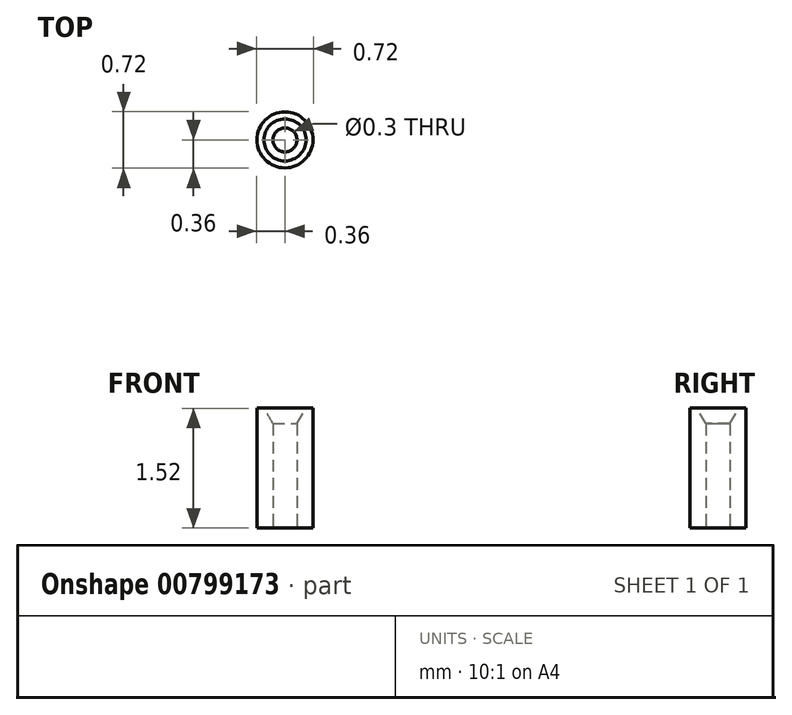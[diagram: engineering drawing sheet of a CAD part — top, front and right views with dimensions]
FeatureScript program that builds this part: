
annotation { "Feature Type Name" : "Feature", "Feature Type Description" : "" }
export const myFeature = defineFeature(function(context is Context, id is Id, definition is map)
    precondition{}
    {
        {
            var Q0;
            Q0=qCreatedBy(makeId("Front.planeOp"),FACE);
            var sketch = newSketch(context, id + "F0", { "sketchPlane" : qUnion([Q0])});
            skLineSegment(sketch, "E0", {"start": v(0.15, 0) * mm, "end": v(0.15, 1.33) * mm});
            skLineSegment(sketch, "E1", {"start": v(0.15, 1.33) * mm, "end": v(0.27, 1.52) * mm});
            skLineSegment(sketch, "E2", {"start": v(0.27, 1.52) * mm, "end": v(0.36, 1.52) * mm});
            skLineSegment(sketch, "E3", {"start": v(0.36, 1.52) * mm, "end": v(0.36, 0) * mm});
            skLineSegment(sketch, "E4", {"start": v(0.36, 0) * mm, "end": v(0.15, 0) * mm});
            skLineSegment(sketch, "E5", {"start": v(0, 0) * mm, "end": v(0, 1.52) * mm, "construction": true});
            skSolve(sketch);
        }
        {
            var Q0;
            Q0=qSketchRegion(id+"F0",true);
            var Q1;
            Q1=sQuery(id+"F0.wireOp",EDGE,"E5");
            revolve(context, id + "F1", {"entities" : qUnion([Q0]), "axis" : qUnion([Q1]), "revolveType" : RevolveType.FULL});
        }
    });
